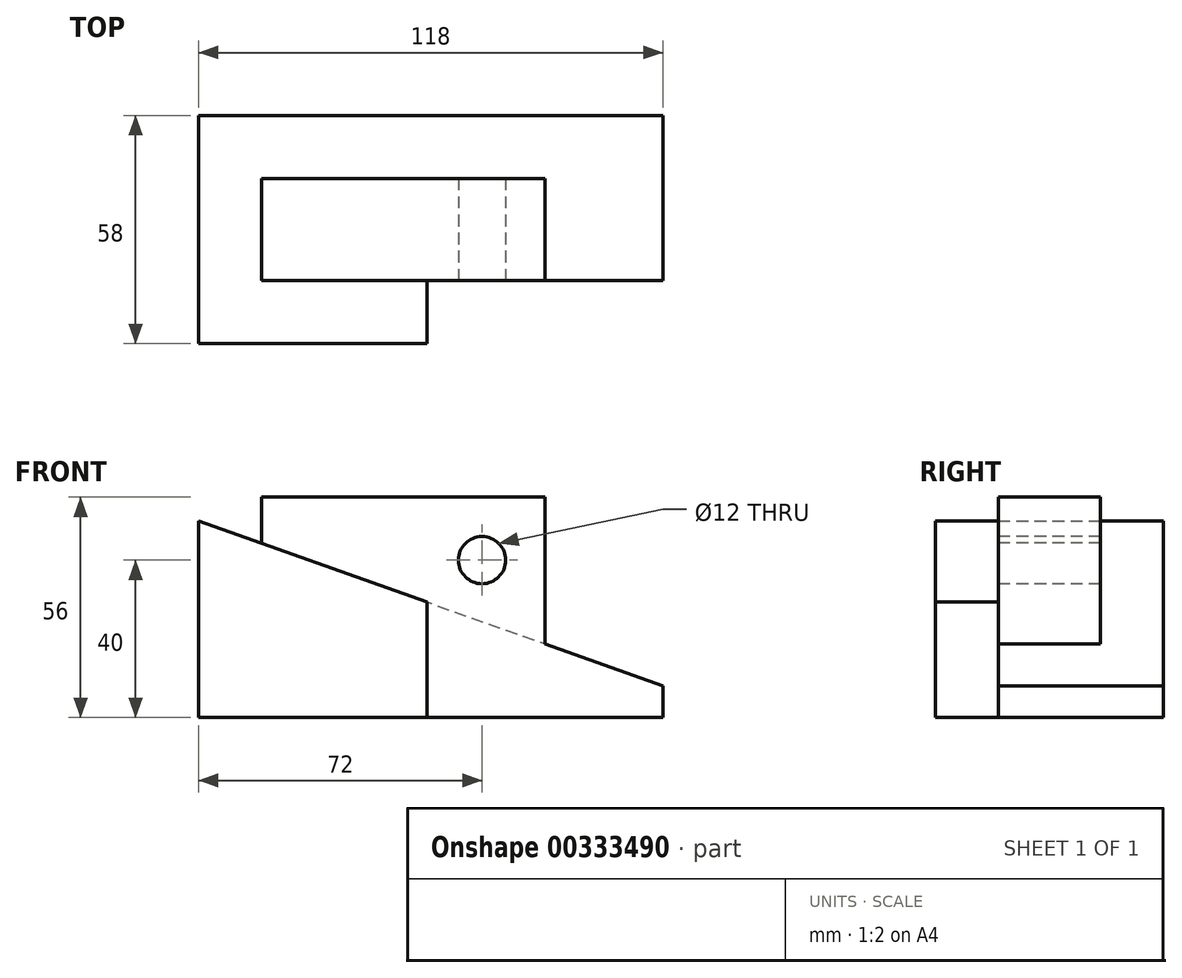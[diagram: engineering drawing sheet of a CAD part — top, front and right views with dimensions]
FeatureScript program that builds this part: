
annotation { "Feature Type Name" : "Feature", "Feature Type Description" : "" }
export const myFeature = defineFeature(function(context is Context, id is Id, definition is map)
    precondition{}
    {
        {
            var Q0;
            Q0=qCreatedBy(makeId("Top.planeOp"),FACE);
            var sketch = newSketch(context, id + "F0", { "sketchPlane" : qUnion([Q0])});
            skLineSegment(sketch, "E0", {"start": v(0, 0) * mm, "end": v(0, 58) * mm});
            skLineSegment(sketch, "E1", {"start": v(0, 58) * mm, "end": v(118, 58) * mm});
            skLineSegment(sketch, "E2", {"start": v(118, 58) * mm, "end": v(118, 16) * mm});
            skLineSegment(sketch, "E3", {"start": v(118, 16) * mm, "end": v(58, 16) * mm});
            skLineSegment(sketch, "E4", {"start": v(58, 16) * mm, "end": v(58, 0) * mm});
            skLineSegment(sketch, "E5", {"start": v(58, 0) * mm, "end": v(0, 0) * mm});
            skLineSegment(sketch, "E6", {"start": v(58, 16) * mm, "end": v(88, 16) * mm});
            skLineSegment(sketch, "E7", {"start": v(88, 16) * mm, "end": v(88, 42) * mm});
            skLineSegment(sketch, "E8", {"start": v(88, 42) * mm, "end": v(16, 42) * mm});
            skLineSegment(sketch, "E9", {"start": v(16, 42) * mm, "end": v(16, 16) * mm});
            skLineSegment(sketch, "E10", {"start": v(16, 16) * mm, "end": v(88, 16) * mm});
            skSolve(sketch);
        }
        {
            var Q0;
            Q0=makeQuery(id+"F0.imprint","IMPRINT",FACE,{"disambiguationData":[TD([[makeQuery(id+"F0.imprint","IMPRINT",EDGE,{"derivedFrom":sQuery(id+"F0.wireOp",EDGE,"E0")}),-1.0]])]});
            extrude(context, id + "F1", {"entities" : qUnion([Q0]), "depth" : 50 * mm});
        }
        {
            var Q0;
            Q0=makeQuery(id+"F1.opExtrude","SWEPT_FACE",FACE,{"disambiguationData":[OSD([sQuery(id+"F0.wireOp",EDGE,"E1")])]});
            var sketch = newSketch(context, id + "F2", { "sketchPlane" : qUnion([Q0])});
            skLineSegment(sketch, "E11", {"start": v(-118, 50) * mm, "end": v(0, 50) * mm});
            skLineSegment(sketch, "E12", {"start": v(0, 50) * mm, "end": v(-118, 8) * mm});
            skLineSegment(sketch, "E13", {"start": v(-118, 8) * mm, "end": v(-118, 50) * mm});
            skSolve(sketch);
        }
        {
            var Q0;
            Q0 = qSketchRegion(id + "F2", true);
            extrude(context, id + "F3", {"entities" : qUnion([Q0]), "operationType" : NewBodyOperationType.REMOVE, "endBound" : BoundingType.THROUGH_ALL, "oppositeDirection" : true, "depth" : 25 * mm});
        }
        {
            var Q0;
            {var subQ3=sQuery(id+"F0.wireOp",EDGE,"E7");Q0=makeQuery(id+"F0.imprint","IMPRINT",FACE,{"disambiguationData":[TD([[makeQuery(id+"F0.imprint","IMPRINT",EDGE,{"derivedFrom":subQ3}),1.0]])]});}
            extrude(context, id + "F4", {"entities" : qUnion([Q0]), "operationType" : NewBodyOperationType.ADD, "depth" : 56 * mm});
        }
        {
            var Q0;
            Q0=makeQuery(id+"F4.boolean.opBoolean","MERGE",FACE,{"derivedFrom":[makeQuery(id+"F1.opExtrude","SWEPT_FACE",FACE,{"disambiguationData":[OSD([sQuery(id+"F0.wireOp",EDGE,"E3")])]}),makeQuery(id+"F4.opExtrude","SWEPT_FACE",FACE,{"disambiguationData":[OSD([sQuery(id+"F0.wireOp",EDGE,"E10")])]})]});
            var sketch = newSketch(context, id + "F5", { "sketchPlane" : qUnion([Q0])});
            skCircle(sketch, "E14", {"center": v(72, 40) * mm, "radius": 6 * mm});
            skSolve(sketch);
        }
        {
            var Q0;
            Q0 = qSketchRegion(id + "F5", true);
            extrude(context, id + "F6", {"entities" : qUnion([Q0]), "operationType" : NewBodyOperationType.REMOVE, "oppositeDirection" : true, "depth" : 26 * mm});
        }
    });
